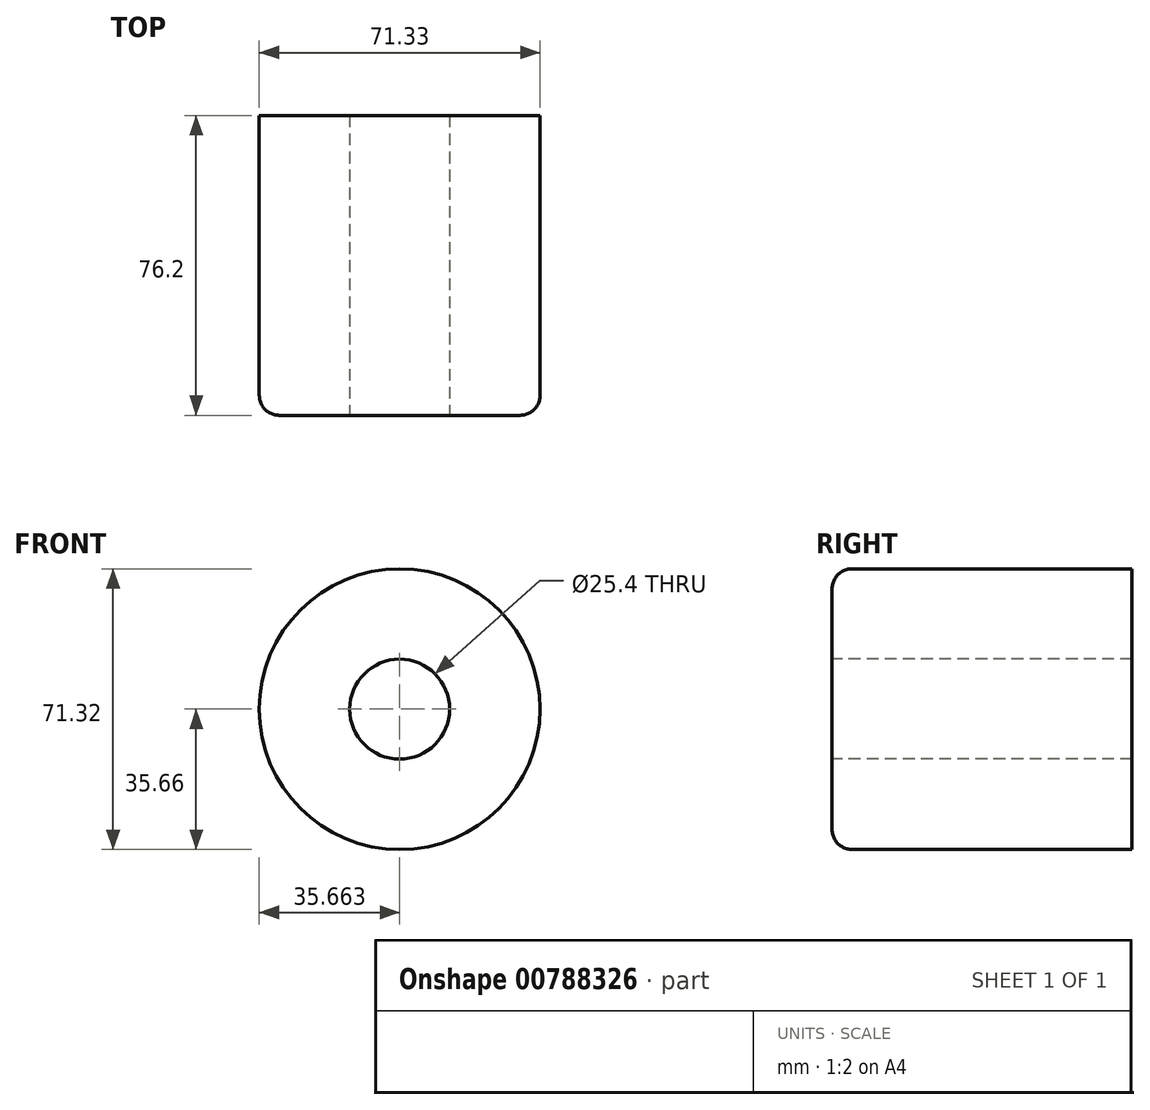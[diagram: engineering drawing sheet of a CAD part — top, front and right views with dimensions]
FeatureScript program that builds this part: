
annotation { "Feature Type Name" : "Feature", "Feature Type Description" : "" }
export const myFeature = defineFeature(function(context is Context, id is Id, definition is map)
    precondition{}
    {
        {
            var Q0;
            Q0=qCreatedBy(makeId("Front.planeOp"),FACE);
            var sketch = newSketch(context, id + "F0", { "sketchPlane" : qUnion([Q0])});
            skCircle(sketch, "E0", {"center": v(-92.19, 32.67) * mm, "radius": 35.66 * mm});
            skSolve(sketch);
        }
        {
            var Q0;
            Q0=makeQuery(id+"F0.imprint","IMPRINT",FACE,{"disambiguationData":[TD([[makeQuery(id+"F0.imprint","IMPRINT",EDGE,{"derivedFrom":sQuery(id+"F0.wireOp",EDGE,"E0")}),1.0]])]});
            extrude(context, id + "F1", {"entities" : qUnion([Q0]), "oppositeDirection" : true, "depth" : 76.2 * mm, "offsetDistance" : 25.4 * mm});
        }
        {
            var Q0;
            Q0=makeQuery(id+"F1.opExtrude","CAP_FACE",FACE,{"disambiguationData":[OSD([sQuery(id+"F0.wireOp",EDGE,"E0")])],"isStart":true});
            var sketch = newSketch(context, id + "F2", { "sketchPlane" : qUnion([Q0])});
            skCircle(sketch, "E1", {"center": v(-92.19, 32.67) * mm, "radius": 26.48 * mm});
            skSolve(sketch);
        }
        {
            var Q0;
            Q0=sQuery(id+"F2.wireOp",VERTEX,"E1.center");
            var Q1;
            Q1=makeQuery(id+"F1.opExtrude","SWEPT_BODY",BODY,{"disambiguationData":[OSD([sQuery(id+"F0.wireOp",EDGE,"E0")])]});
            hole(context, id + "F3", {"style" : HoleStyle.SIMPLE, "endStyle" : HoleEndStyle.THROUGH, "holeDiameter" : 25.4 * mm, "majorDiameter" : 6.35 * mm, "isTappedThrough" : true, "tappedDepth" : 12.7 * mm, "tapClearance" : 3, "locations" : qUnion([Q0]), "scope" : qUnion([Q1])});
        }
        {
            var Q0;
            Q0=makeQuery(id+"F1.opExtrude","CAP_EDGE",EDGE,{"disambiguationData":[OSD([sQuery(id+"F0.wireOp",EDGE,"E0")])],"isStart":true});
            fillet(context, id + "F4", {"entities" : qUnion([Q0]), "radius" : 5.08 * mm, "tangentPropagation" : true, "allowEdgeOverflow" : false});
        }
    });
